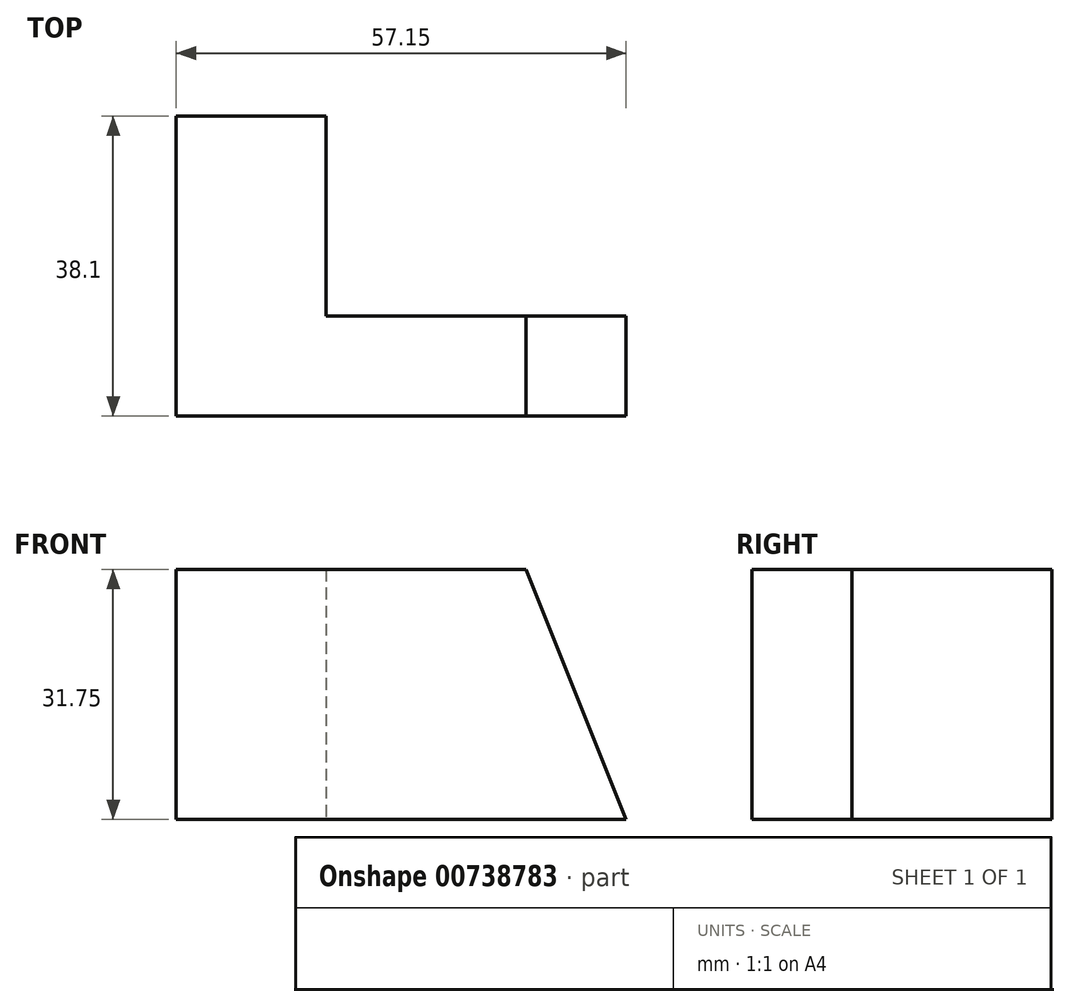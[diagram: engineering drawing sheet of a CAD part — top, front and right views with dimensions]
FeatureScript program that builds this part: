
annotation { "Feature Type Name" : "Feature", "Feature Type Description" : "" }
export const myFeature = defineFeature(function(context is Context, id is Id, definition is map)
    precondition{}
    {
        {
            var Q0;
            Q0=qCreatedBy(makeId("Front.planeOp"),FACE);
            var sketch = newSketch(context, id + "F0", { "sketchPlane" : qUnion([Q0])});
            skLineSegment(sketch, "E0", {"start": v(0, 0) * mm, "end": v(0, 31.75) * mm});
            skLineSegment(sketch, "E1", {"start": v(0, 31.75) * mm, "end": v(57.15, 31.75) * mm});
            skLineSegment(sketch, "E2", {"start": v(57.15, 31.75) * mm, "end": v(57.15, 0) * mm});
            skLineSegment(sketch, "E3", {"start": v(57.15, 0) * mm, "end": v(0, 0) * mm});
            skSolve(sketch);
        }
        {
            var Q0;
            Q0 = qSketchRegion(id + "F0", true);
            extrude(context, id + "F1", {"entities" : qUnion([Q0]), "depth" : 38.1 * mm, "offsetDistance" : 25.4 * mm});
        }
        {
            var Q0;
            Q0=qCreatedBy(makeId("Front.planeOp"),FACE);
            var sketch = newSketch(context, id + "F2", { "sketchPlane" : qUnion([Q0])});
            skLineSegment(sketch, "E4", {"start": v(19.05, 31.75) * mm, "end": v(31.75, 0) * mm});
            skLineSegment(sketch, "E5", {"start": v(31.75, 0) * mm, "end": v(57.15, 0) * mm});
            skLineSegment(sketch, "E6", {"start": v(57.15, 0) * mm, "end": v(44.45, 31.75) * mm});
            skLineSegment(sketch, "E7", {"start": v(44.45, 31.75) * mm, "end": v(19.05, 31.75) * mm});
            skSolve(sketch);
        }
        {
            var Q0;
            Q0 = qSketchRegion(id + "F2", true);
            extrude(context, id + "F3", {"entities" : qUnion([Q0]), "operationType" : NewBodyOperationType.REMOVE, "depth" : 12.7 * mm, "offsetDistance" : 25.4 * mm});
        }
        {
            var Q0;
            {var subQ0=sQuery(id+"F0.wireOp",EDGE,"E1");var subQ1=sQuery(id+"F0.wireOp",EDGE,"E2");Q0=makeQuery(id+"F3.boolean.opBoolean","SPLIT",FACE,{"disambiguationData":[TD([makeQuery(id+"F1.opExtrude","SWEPT_FACE",FACE,{"disambiguationData":[OSD([subQ1])]})])],"derivedFrom":makeQuery(id+"F1.opExtrude","CAP_FACE",FACE,{"disambiguationData":[OSD([sQuery(id+"F0.wireOp",EDGE,"E0"),subQ0,subQ1,sQuery(id+"F0.wireOp",EDGE,"E3")])],"isStart":true})});}
            extrude(context, id + "F4", {"entities" : qUnion([Q0]), "operationType" : NewBodyOperationType.REMOVE, "oppositeDirection" : true, "depth" : 38.1 * mm, "offsetDistance" : 25.4 * mm});
        }
        {
            var Q0;
            Q0=qCreatedBy(makeId("Front.planeOp"),FACE);
            var sketch = newSketch(context, id + "F5", { "sketchPlane" : qUnion([Q0])});
            skLineSegment(sketch, "E8", {"start": v(44.45, 31.75) * mm, "end": v(57.15, 0) * mm});
            skLineSegment(sketch, "E9", {"start": v(44.45, 31.75) * mm, "end": v(19.05, 31.75) * mm});
            skLineSegment(sketch, "E10", {"start": v(19.05, 31.75) * mm, "end": v(19.05, 0) * mm});
            skLineSegment(sketch, "E11", {"start": v(19.05, 0) * mm, "end": v(57.15, 0) * mm});
            skSolve(sketch);
        }
        {
            var Q0;
            Q0=makeQuery(id+"F5.imprint","IMPRINT",FACE,{"disambiguationData":[TD([[makeQuery(id+"F5.imprint","IMPRINT",EDGE,{"derivedFrom":sQuery(id+"F5.wireOp",EDGE,"E8")}),-1.0]])]});
            extrude(context, id + "F6", {"entities" : qUnion([Q0]), "operationType" : NewBodyOperationType.REMOVE, "depth" : 12.7 * mm, "offsetDistance" : 25.4 * mm});
        }
        {
            var Q0;
            Q0=makeQuery(id+"F6.boolean.opBoolean","MERGE",FACE,{"derivedFrom":[makeQuery(id+"F3.boolean.opBoolean","COPY",FACE,{"derivedFrom":makeQuery(id+"F3.opExtrude","CAP_FACE",FACE,{"disambiguationData":[OSD([sQuery(id+"F2.wireOp",EDGE,"E4"),sQuery(id+"F2.wireOp",EDGE,"E5"),sQuery(id+"F2.wireOp",EDGE,"E6"),sQuery(id+"F2.wireOp",EDGE,"E7")])],"isStart":false})}),makeQuery(id+"F6.opExtrude","CAP_FACE",FACE,{"disambiguationData":[OSD([sQuery(id+"F5.wireOp",EDGE,"E8"),sQuery(id+"F5.wireOp",EDGE,"E9"),sQuery(id+"F5.wireOp",EDGE,"E10"),sQuery(id+"F5.wireOp",EDGE,"E11")])],"isStart":false})]});
            var sketch = newSketch(context, id + "F7", { "sketchPlane" : qUnion([Q0])});
            skLineSegment(sketch, "E12", {"start": v(-19.05, 31.75) * mm, "end": v(-19.05, 0) * mm});
            skLineSegment(sketch, "E13", {"start": v(-19.05, 0) * mm, "end": v(-57.15, 0) * mm});
            skLineSegment(sketch, "E14", {"start": v(-57.15, 0) * mm, "end": v(-44.45, 31.75) * mm});
            skLineSegment(sketch, "E15", {"start": v(-44.45, 31.75) * mm, "end": v(-19.05, 31.75) * mm});
            skSolve(sketch);
        }
        {
            var Q0;
            Q0 = qSketchRegion(id + "F7", true);
            extrude(context, id + "F8", {"entities" : qUnion([Q0]), "operationType" : NewBodyOperationType.REMOVE, "depth" : 12.7 * mm, "offsetDistance" : 25.4 * mm});
        }
        {
            var Q0;
            Q0=makeQuery(id+"F6.boolean.opBoolean","MERGE",FACE,{"derivedFrom":[makeQuery(id+"F3.boolean.opBoolean","COPY",FACE,{"derivedFrom":makeQuery(id+"F3.opExtrude","CAP_FACE",FACE,{"disambiguationData":[OSD([sQuery(id+"F2.wireOp",EDGE,"E4"),sQuery(id+"F2.wireOp",EDGE,"E5"),sQuery(id+"F2.wireOp",EDGE,"E6"),sQuery(id+"F2.wireOp",EDGE,"E7")])],"isStart":false})}),makeQuery(id+"F6.opExtrude","CAP_FACE",FACE,{"disambiguationData":[OSD([sQuery(id+"F5.wireOp",EDGE,"E8"),sQuery(id+"F5.wireOp",EDGE,"E9"),sQuery(id+"F5.wireOp",EDGE,"E10"),sQuery(id+"F5.wireOp",EDGE,"E11")])],"isStart":false})]});
            extrude(context, id + "F9", {"entities" : qUnion([Q0]), "operationType" : NewBodyOperationType.REMOVE, "oppositeDirection" : true, "depth" : 12.7 * mm, "offsetDistance" : 25.4 * mm});
        }
    });
